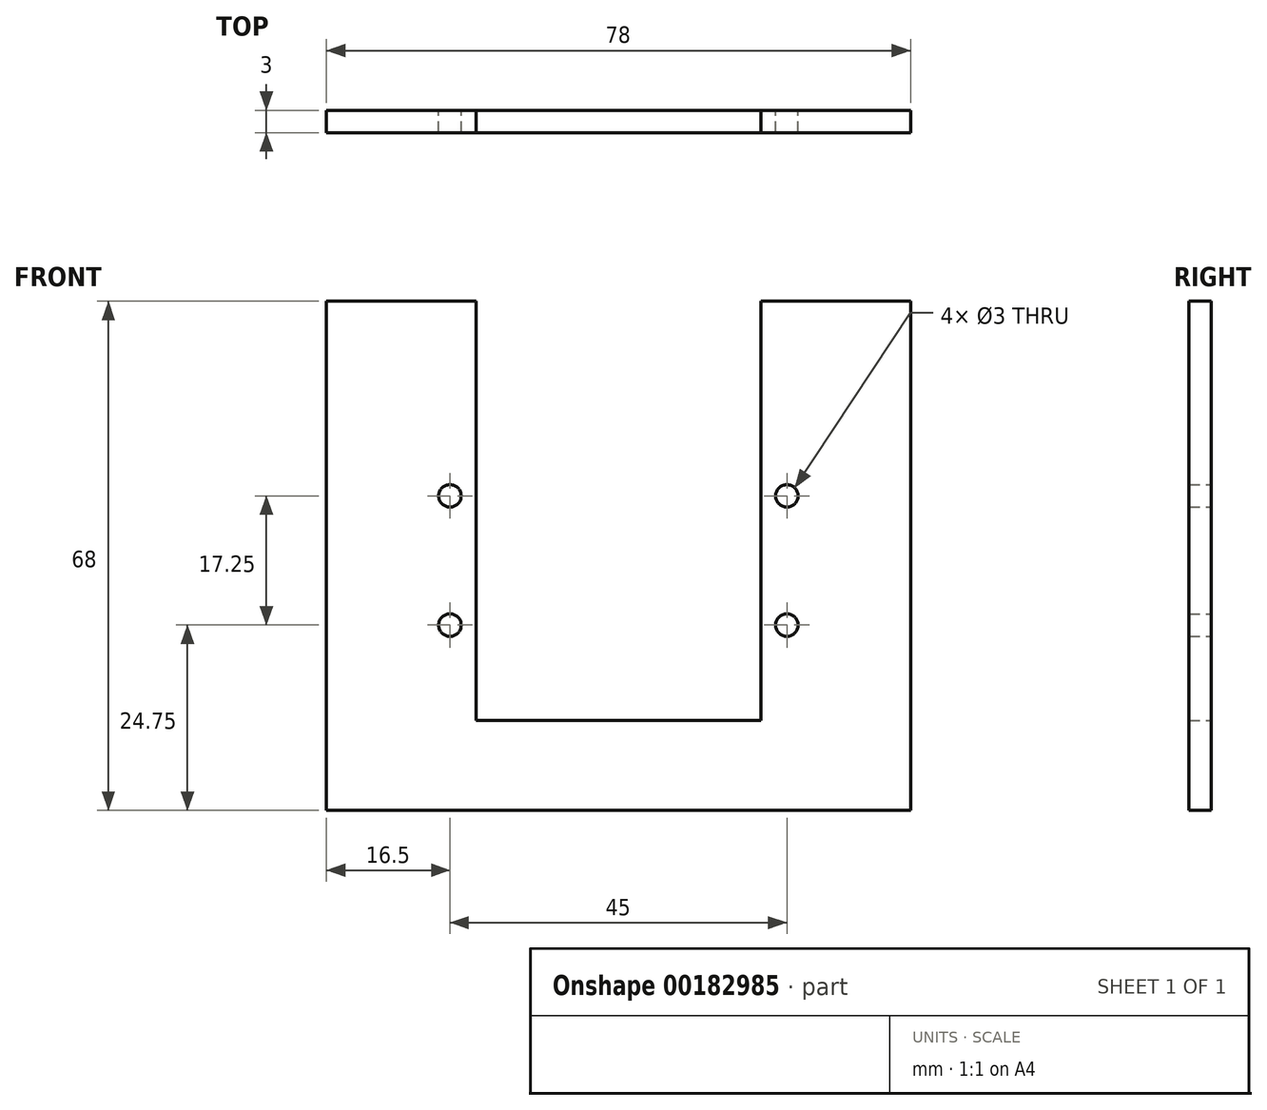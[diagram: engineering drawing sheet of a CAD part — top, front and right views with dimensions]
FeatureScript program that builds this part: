
annotation { "Feature Type Name" : "Feature", "Feature Type Description" : "" }
export const myFeature = defineFeature(function(context is Context, id is Id, definition is map)
    precondition{}
    {
        {
            var Q0;
            Q0=qCreatedBy(makeId("Front.planeOp"), FACE);
            var sketch = newSketch(context, id + "F0", { "sketchPlane" : qUnion([Q0])});
            skLineSegment(sketch, "E0.bottom", {"start": v(39, -34) * mm, "end": v(-39, -34) * mm});
            skLineSegment(sketch, "E0.top", {"start": v(39, 34) * mm, "end": v(19, 34) * mm});
            skLineSegment(sketch, "E0.left", {"start": v(39, -34) * mm, "end": v(39, 34) * mm});
            skLineSegment(sketch, "E0.right", {"start": v(-39, -34) * mm, "end": v(-39, 34) * mm});
            skPoint(sketch, "E0.middle", {"position": v(0, 0) * mm});
            skLineSegment(sketch, "E1.left", {"start": v(19, -19.58) * mm, "end": v(19, 19.58) * mm});
            skLineSegment(sketch, "E1.right", {"start": v(-19, -19.58) * mm, "end": v(-19, 19.58) * mm});
            skLineSegment(sketch, "E2", {"start": v(-19, 19.58) * mm, "end": v(-19, 34) * mm});
            skLineSegment(sketch, "E3", {"start": v(19, 34) * mm, "end": v(19, 19.58) * mm});
            skLineSegment(sketch, "E4.trimOffspring", {"start": v(-19, 34) * mm, "end": v(-39, 34) * mm});
            skLineSegment(sketch, "E5", {"start": v(-19, -22) * mm, "end": v(19, -22) * mm});
            skLineSegment(sketch, "E6", {"start": v(-19, -19.58) * mm, "end": v(-19, -22) * mm});
            skLineSegment(sketch, "E7", {"start": v(19, -19.58) * mm, "end": v(19, -22) * mm});
            skPoint(sketch, "E8.start.orphan", {"position": v(19, -34) * mm});
            skPoint(sketch, "E9.start.orphan", {"position": v(-19, -34) * mm});
            skPoint(sketch, "E10.top.start.orphan", {"position": v(23.9, 16.71) * mm});
            skPoint(sketch, "E11.orphan", {"position": v(23.9, -16.71) * mm});
            skPoint(sketch, "E10.bottom.end.orphan", {"position": v(-23.9, -16.71) * mm});
            skPoint(sketch, "E12.trimOffspring.end.orphan", {"position": v(-23.9, 16.71) * mm});
            skCircle(sketch, "E13", {"center": v(22.5, 8) * mm, "radius": 1.5 * mm});
            skCircle(sketch, "E14.MirrorC", {"center": v(-22.5, 8) * mm, "radius": 1.5 * mm});
            skCircle(sketch, "E15", {"center": v(-22.5, -9.25) * mm, "radius": 1.5 * mm});
            skCircle(sketch, "E16.MirrorC", {"center": v(22.5, -9.25) * mm, "radius": 1.5 * mm});
            skPoint(sketch, "E17.start.orphan", {"position": v(26, 8) * mm});
            skPoint(sketch, "E18.orphan", {"position": v(-26, 15) * mm});
            skPoint(sketch, "E19.trimOffspring.end.orphan", {"position": v(-26, -15) * mm});
            skPoint(sketch, "E20.orphan", {"position": v(26, -15) * mm});
            skPoint(sketch, "E21.top.start.orphan", {"position": v(26, 15) * mm});
            skPoint(sketch, "E22.end.orphan", {"position": v(19, 8) * mm});
            skSolve(sketch);
        }
        {
            var Q0;
            Q0 = qSketchRegion(id + "F0", true);
            extrude(context, id + "F1", {"entities" : qUnion([Q0]), "depth" : 3 * mm, "offsetDistance" : 25 * mm});
        }
    });
